# Revit family: 10-E055-DC-CL
name_source: partatom
category: Luminarias
revit_build: Autodesk Revit 2017 (Build: 20160225_1515(x64)
units: mm (PartAtom-declared; Revit-internal decimal feet)

## family parameters
Compartido = Sí
Corte con vacíos al cargar = No
Cota de conector redondo = Diámetro de uso
Número OmniClass = 23.80.70.00
Origen de luz = No
Punto de cálculo de habitación = No
Se basa en plano de trabajo = No
Siempre vertical = Sí
Tipo de pieza = Normal
Título OmniClass = Lighting

## types (1)
- 10-E055-DC-CL
    Acabado = Cemento, Opal
    CRI = 80
    Catálogo = Outdoor
    CodigoGubimclass = 50.60.50.20
    CodigoOmniclass = 21-04 50 40
    CodigoUniclass2015 = EF_70_80
    CodigoUniformat2010 = D5040
    DescripcionGubimclass = Iluminación interior
    DescripcionOmniclass = Lighting
    DescripcionUniclass2015 = Lighting
    DescripcionUniformat2010 = Lighting
    EAN13 = 8435526873791
    Eficiencia energética = LED A++
    Etiqueta V/f = 100-240V/50-60Hz
    Fabricante = LEDS C4
    Familia = Row 230mm
    FechaVersion = Julio 2020
    Ficha = http://files.leds-c4.com
    Fotometría = http://files.leds-c4.com
    Fuente de luz = 60xLED 17.4 2585.00 lm
    IK = IK10
    IMC = http://files.leds-c4.com
    IP = IP65
    IfcExportAs = IfcLightFixture
    IfcExportType = NOTDEFINED
    Imagen web = http://files.leds-c4.com
    LDT = http://files.leds-c4.com
    Lumenes reales (lm) = 1071
    Material = Cemento, Policarbonato
    Peso neto (KG) = 5.44
    Pluma comercial = http://files.leds-c4.com
    Producto descatalogado = Catalogado ES
    Rayo de luz = Check Photometric file
    Referencia = 10-E055-DC-CL
    Temperatura color led (K) = Blanco cálido - 3000K
    Tender text (Castellano) = LEDS C4
Row 230mm
10-E055-DC-CL

Aplique de uso exterior para iluminar hacia abajo. 

Incluye base con &quot;PRO-base SYSTEM&quot; para garantizar una instalación perfecta y una mayor estabilidad y durabilidad de la luminaria. Apto para instalar en ambientes con atmósfera marina. Incluye 2 salidas de cable para facilitar la instalación en cadena. Material estructura: Cemento. Acabado estructura: Cemento. Material difusor: Policarbonato. Acabado difusor: Opal. Protección contra los rayos ultravioleta. Garantía: 5 Años.

Peso neto del producto (Kg): 5.440
Anchura o diámetro del producto (mm): 160
Altura del producto (mm): 230

Clase 1. IP: IP65. IK: IK10. LED. Nº de portalámparas o Leds: 60. Marca del LED: SAMSUNG. Marca del Driver: HEP. Potencia máxima de la fuente de luz: 17.4W. Temperatura de color: Blanco cálido - 3000K. Índice de reproducción cromática: 80. Steps Mac Adam: 3. Diámetro máximo de la bombilla que admite la luminaria: 50.000h L80B20. UGR:  23.3. Riesgo fotobiológico: RG0. Flujo real (lm): 1071. Flujo nominal (lm): 2585. Lm/W reales: 55. Rango de voltaje/frecuencia: 100-277 VAC. Voltaje: 6. Equipo incluido: Si, electrónico. Potencia total: 19.3. Factor de potencia: 0.91.
    Tender text (English) = LEDS C4
Row 230mm
10-E055-DC-CL

Wall light for outdoor use. 

For downlighting. Includes base with &quot;PRO-base SYSTEM&quot; to ensure perfect installation and make the light more stable and durable. Suitable for installation in marine environments. Includes 2 cable outlets to facilitate chain mounting. Structure material: cement. Structure finish: Cement. Diffuser material: Polycarbonate. Diffuser finish: Opal. UV protection. Warranty: 5 Years.

Product net weight (Kg): 5.440
Product width or diameter (mm): 160
Product height (mm): 230

Class 1. IP: IP65. IK: IK10. LED. No. of lampholders or LEDs: 60. LED brand: SAMSUNG. Driver brand: HEP. Maximum power of light source: 17.4W. Colour temperature: LED warm-white 3000K. Colour rendering index: 80. MacAdam Steps: 3. Maximum diameter of luminaire bulb: 50.000h L80B20. UGR:  23.3. Photobiological risk: RG0. Real flux (lm): 1071. Nominal flux (lm): 2585. Lm/Real W: 55. Voltage and frequency range: 100-277 VAC. Voltage: 6. Gear included: Yes, electronic. Total power: 19.3. Power factor: 0.91.
    Tipo = Baliza
    Vatios (W) = 19.3
    Versión = v1
